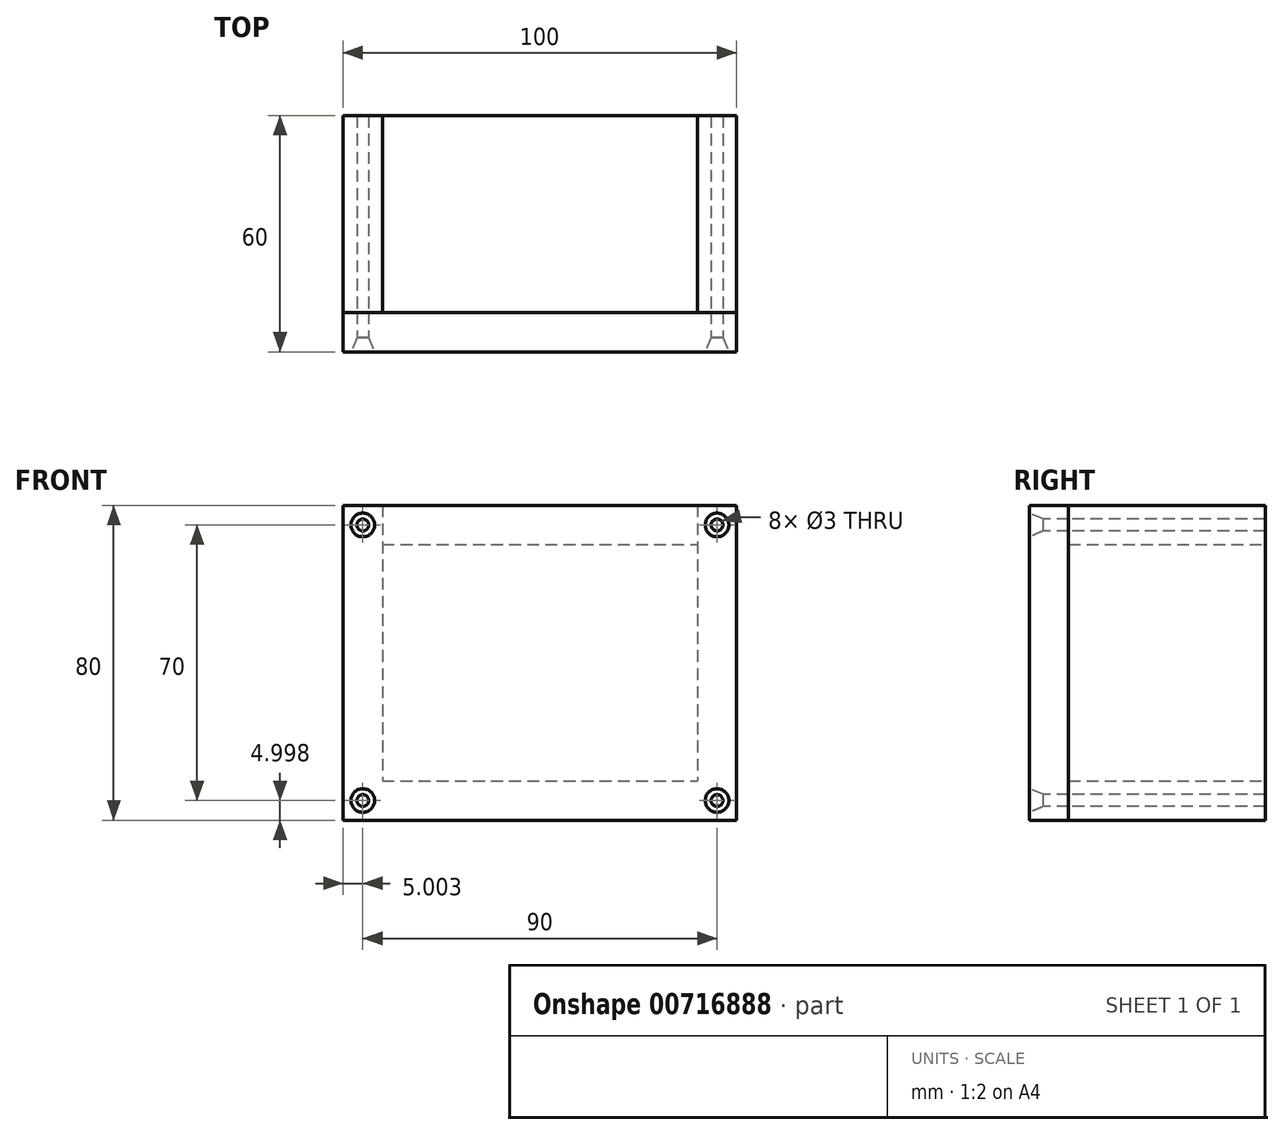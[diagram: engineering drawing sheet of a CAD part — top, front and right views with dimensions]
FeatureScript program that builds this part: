
annotation { "Feature Type Name" : "Feature", "Feature Type Description" : "" }
export const myFeature = defineFeature(function(context is Context, id is Id, definition is map)
    precondition{}
    {
        {
            var Q0;
            Q0=qCreatedBy(makeId("Front.planeOp"),FACE);
            var sketch = newSketch(context, id + "F0", { "sketchPlane" : qUnion([Q0])});
            skLineSegment(sketch, "E0", {"start": v(60.77, 44.99) * mm, "end": v(-29.23, 44.99) * mm});
            skLineSegment(sketch, "E1", {"start": v(-29.23, 44.99) * mm, "end": v(-29.23, -35.01) * mm});
            skLineSegment(sketch, "E2", {"start": v(-29.23, 44.99) * mm, "end": v(-19.23, 44.99) * mm});
            skLineSegment(sketch, "E3", {"start": v(-19.23, 44.99) * mm, "end": v(-19.23, 34.99) * mm});
            skLineSegment(sketch, "E4", {"start": v(-19.23, 34.99) * mm, "end": v(-19.23, -35.01) * mm});
            skLineSegment(sketch, "E5", {"start": v(-19.23, 34.99) * mm, "end": v(60.77, 34.99) * mm});
            skLineSegment(sketch, "E6", {"start": v(60.77, 44.99) * mm, "end": v(60.77, -35.01) * mm});
            skLineSegment(sketch, "E7", {"start": v(-29.23, -35.01) * mm, "end": v(60.77, -35.01) * mm});
            skPoint(sketch, "E8.orphan", {"position": v(-29.23, -46.73) * mm});
            skPoint(sketch, "E9.end.orphan", {"position": v(29.92, -46.73) * mm});
            skLineSegment(sketch, "E10", {"start": v(-19.23, -35.01) * mm, "end": v(-19.23, -25.01) * mm});
            skLineSegment(sketch, "E11", {"start": v(-19.23, -25.01) * mm, "end": v(60.77, -25.01) * mm});
            skLineSegment(sketch, "E12", {"start": v(60.77, 44.99) * mm, "end": v(70.77, 44.99) * mm});
            skLineSegment(sketch, "E13", {"start": v(70.77, 44.99) * mm, "end": v(70.77, -35.01) * mm});
            skLineSegment(sketch, "E14", {"start": v(60.77, -35.01) * mm, "end": v(70.77, -35.01) * mm});
            skSolve(sketch);
        }
        {
            var Q0;
            {var subQ3=sQuery(id+"F0.wireOp",EDGE,"E3");Q0=makeQuery(id+"F0.imprint","IMPRINT",FACE,{"disambiguationData":[TD([[makeQuery(id+"F0.imprint","IMPRINT",EDGE,{"derivedFrom":subQ3}),1.0]])]});}
            var sketch = newSketch(context, id + "F1", { "sketchPlane" : qUnion([Q0])});
            skSolve(sketch);
        }
        {
            var Q0;
            {var subQ3=sQuery(id+"F0.wireOp",EDGE,"E3");Q0=makeQuery(id+"F1.imprint","IMPRINT",FACE,{"disambiguationData":[TD([[makeQuery(id+"F1.imprint","IMPRINT",EDGE,{"derivedFrom":makeQuery(id+"F0.imprint","IMPRINT",EDGE,{"derivedFrom":subQ3})}),1.0]])]});}
            var sketch = newSketch(context, id + "F2", { "sketchPlane" : qUnion([Q0])});
            skSolve(sketch);
        }
        {
            var Q0;
            Q0=qCreatedBy(makeId("Front.planeOp"),FACE);
            var sketch = newSketch(context, id + "F3", { "sketchPlane" : qUnion([Q0])});
            skSolve(sketch);
        }
        {
            var Q0;
            Q0 = qSketchRegion(id + "F3", true);
            var Q1;
            {var subQ3=sQuery(id+"F0.wireOp",EDGE,"E1");Q1=makeQuery(id+"F0.imprint","IMPRINT",FACE,{"disambiguationData":[TD([[makeQuery(id+"F0.imprint","IMPRINT",EDGE,{"derivedFrom":subQ3}),1.0]])]});}
            var Q2;
            {var subQ3=sQuery(id+"F0.wireOp",EDGE,"E3");Q2=makeQuery(id+"F2.imprint","IMPRINT",FACE,{"disambiguationData":[TD([[makeQuery(id+"F2.imprint","IMPRINT",EDGE,{"derivedFrom":makeQuery(id+"F1.imprint","IMPRINT",EDGE,{"derivedFrom":makeQuery(id+"F0.imprint","IMPRINT",EDGE,{"derivedFrom":subQ3})})}),1.0]])]});}
            var Q3;
            {var subQ3=sQuery(id+"F0.wireOp",EDGE,"E12");Q3=makeQuery(id+"F0.imprint","IMPRINT",FACE,{"disambiguationData":[TD([[makeQuery(id+"F0.imprint","IMPRINT",EDGE,{"derivedFrom":subQ3}),-1.0]])]});}
            var Q4;
            {var subQ3=sQuery(id+"F0.wireOp",EDGE,"E11");Q4=makeQuery(id+"F0.imprint","IMPRINT",FACE,{"disambiguationData":[TD([[makeQuery(id+"F0.imprint","IMPRINT",EDGE,{"derivedFrom":subQ3}),-1.0]])]});}
            extrude(context, id + "F4", {"entities" : qUnion([Q0, Q1, Q2, Q3, Q4]), "depth" : 50 * mm, "offsetDistance" : 25 * mm});
        }
        {
            var Q0;
            Q0=makeQuery(id+"F4.opExtrude","SWEPT_FACE",FACE,{"disambiguationData":[OSD([sQuery(id+"F0.wireOp",EDGE,"E1")])]});
            var sketch = newSketch(context, id + "F5", { "sketchPlane" : qUnion([Q0])});
            skLineSegment(sketch, "E15", {"start": v(50, 44.99) * mm, "end": v(60, 44.99) * mm});
            skLineSegment(sketch, "E16", {"start": v(60, 44.99) * mm, "end": v(60, -35.01) * mm});
            skLineSegment(sketch, "E17", {"start": v(60, -35.01) * mm, "end": v(50, -35.01) * mm});
            skSolve(sketch);
        }
        {
            var Q0;
            Q0 = qSketchRegion(id + "F5", true);
            var Q1;
            Q1=makeQuery(id+"F5.imprint","IMPRINT",FACE,{"disambiguationData":[TD([[makeQuery(id+"F5.imprint","IMPRINT",EDGE,{"derivedFrom":sQuery(id+"F5.wireOp",EDGE,"E15")}),-1.0]])]});
            extrude(context, id + "F6", {"entities" : qUnion([Q0, Q1]), "oppositeDirection" : true, "depth" : 100 * mm, "offsetDistance" : 25 * mm});
        }
        {
            var Q0;
            Q0=makeQuery(id+"F6.opExtrude","SWEPT_FACE",FACE,{"disambiguationData":[OSD([sQuery(id+"F5.wireOp",EDGE,"E16")])]});
            var sketch = newSketch(context, id + "F7", { "sketchPlane" : qUnion([Q0])});
            skLineSegment(sketch, "E18", {"start": v(-29.23, 44.99) * mm, "end": v(-24.23, 44.99) * mm});
            skLineSegment(sketch, "E19", {"start": v(-24.23, 44.99) * mm, "end": v(-24.23, 39.99) * mm});
            skLineSegment(sketch, "E20", {"start": v(70.77, 44.99) * mm, "end": v(65.77, 44.99) * mm});
            skLineSegment(sketch, "E21", {"start": v(65.77, 44.99) * mm, "end": v(65.77, 39.99) * mm});
            skLineSegment(sketch, "E22", {"start": v(-29.23, -35.01) * mm, "end": v(-24.23, -35.01) * mm});
            skLineSegment(sketch, "E23", {"start": v(-24.23, -35.01) * mm, "end": v(-24.23, -30.01) * mm});
            skLineSegment(sketch, "E24", {"start": v(70.77, -35.01) * mm, "end": v(65.77, -35.01) * mm});
            skLineSegment(sketch, "E25", {"start": v(65.77, -35.01) * mm, "end": v(65.77, -30.01) * mm});
            skPoint(sketch, "E26", {"position": v(-24.23, 39.99) * mm});
            skPoint(sketch, "E27", {"position": v(-24.23, -30.01) * mm});
            skPoint(sketch, "E28", {"position": v(65.77, -30.01) * mm});
            skPoint(sketch, "E29", {"position": v(65.77, 39.99) * mm});
            skSolve(sketch);
        }
        {
            var Q0;
            Q0=sQuery(id+"F7.wireOp",VERTEX,"E26");
            var Q1;
            Q1=sQuery(id+"F7.wireOp",VERTEX,"E29");
            var Q2;
            Q2=sQuery(id+"F7.wireOp",VERTEX,"E28");
            var Q3;
            Q3=sQuery(id+"F7.wireOp",VERTEX,"E27");
            var Q4;
            Q4=makeQuery(id+"F6.opExtrude","SWEPT_BODY",BODY,{"disambiguationData":[OSD([sQuery(id+"F0.wireOp",EDGE,"E1"),sQuery(id+"F5.wireOp",EDGE,"E15"),sQuery(id+"F5.wireOp",EDGE,"E16"),sQuery(id+"F5.wireOp",EDGE,"E17")])]});
            var Q5;
            Q5=makeQuery(id+"F4.opExtrude","SWEPT_BODY",BODY,{"disambiguationData":[OSD([sQuery(id+"F0.wireOp",EDGE,"E0"),sQuery(id+"F0.wireOp",EDGE,"E1"),sQuery(id+"F0.wireOp",EDGE,"E3"),sQuery(id+"F0.wireOp",EDGE,"E4"),sQuery(id+"F0.wireOp",EDGE,"E6"),sQuery(id+"F0.wireOp",EDGE,"E7"),sQuery(id+"F0.wireOp",EDGE,"E11"),sQuery(id+"F0.wireOp",EDGE,"E12"),sQuery(id+"F0.wireOp",EDGE,"E13"),sQuery(id+"F0.wireOp",EDGE,"E14")])]});
            hole(context, id + "F8", {"style" : HoleStyle.C_SINK, "endStyle" : HoleEndStyle.THROUGH, "holeDiameter" : 3 * mm, "cSinkDiameter" : 6 * mm, "cSinkAngle" : 45 * degree, "majorDiameter" : 5 * mm, "isTappedThrough" : true, "tappedDepth" : 12 * mm, "tapClearance" : 3, "locations" : qUnion([Q0, Q1, Q2, Q3]), "scope" : qUnion([Q4, Q5])});
        }
    });
